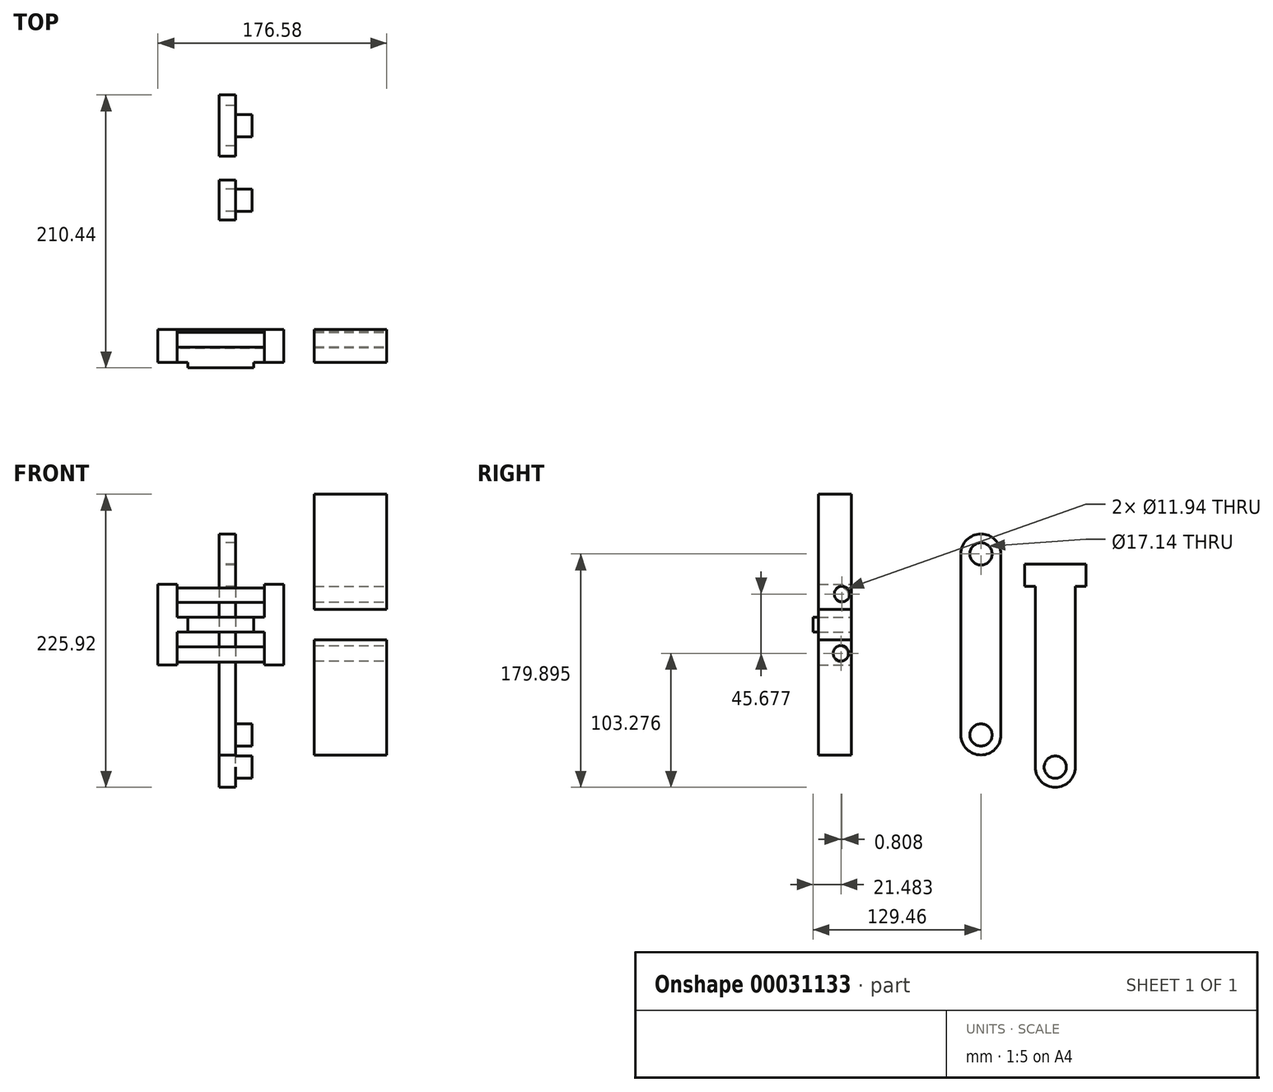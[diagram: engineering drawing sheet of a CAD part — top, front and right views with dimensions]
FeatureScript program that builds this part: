
annotation { "Feature Type Name" : "Feature", "Feature Type Description" : "" }
export const myFeature = defineFeature(function(context is Context, id is Id, definition is map)
    precondition{}
    {
        {
            var Q0;
            Q0=qCreatedBy(makeId("Front.planeOp"),FACE);
            var sketch = newSketch(context, id + "F0", { "sketchPlane" : qUnion([Q0])});
            skLineSegment(sketch, "E0.left", {"start": v(-47.09, 25.12) * mm, "end": v(-47.09, -37.18) * mm});
            skLineSegment(sketch, "E0.right", {"start": v(50.08, 25.12) * mm, "end": v(50.08, -37.18) * mm});
            skLineSegment(sketch, "E1.top", {"start": v(-32.36, -0.3) * mm, "end": v(35.17, -0.3) * mm});
            skLineSegment(sketch, "E1.left", {"start": v(-32.36, 25.12) * mm, "end": v(-32.36, -0.3) * mm});
            skLineSegment(sketch, "E1.right", {"start": v(35.17, 25.12) * mm, "end": v(35.17, -0.3) * mm});
            skLineSegment(sketch, "E2.top", {"start": v(-32.36, -11.75) * mm, "end": v(35.17, -11.75) * mm});
            skLineSegment(sketch, "E2.left", {"start": v(-32.36, -37.18) * mm, "end": v(-32.36, -11.75) * mm});
            skLineSegment(sketch, "E2.right", {"start": v(35.17, -37.18) * mm, "end": v(35.17, -11.75) * mm});
            skLineSegment(sketch, "E3", {"start": v(50.08, 25.12) * mm, "end": v(35.17, 25.12) * mm});
            skLineSegment(sketch, "E4", {"start": v(-32.36, 25.12) * mm, "end": v(-47.09, 25.12) * mm});
            skLineSegment(sketch, "E5", {"start": v(-32.36, -37.18) * mm, "end": v(-47.09, -37.18) * mm});
            skLineSegment(sketch, "E6", {"start": v(50.08, -37.18) * mm, "end": v(35.17, -37.18) * mm});
            skLineSegment(sketch, "E7.trimOffspring", {"start": v(35.17, -37.18) * mm, "end": v(50.08, -37.18) * mm});
            skLineSegment(sketch, "E8.top", {"start": v(73.53, -17.9) * mm, "end": v(129.5, -17.9) * mm});
            skLineSegment(sketch, "E8.left", {"start": v(73.53, -106.8) * mm, "end": v(73.53, -17.9) * mm});
            skLineSegment(sketch, "E8.right", {"start": v(129.5, -106.8) * mm, "end": v(129.5, -17.9) * mm});
            skLineSegment(sketch, "E9.bottom", {"start": v(129.5, 5.5) * mm, "end": v(73.53, 5.5) * mm});
            skLineSegment(sketch, "E9.top", {"start": v(129.5, 94.4) * mm, "end": v(73.53, 94.4) * mm});
            skLineSegment(sketch, "E9.left", {"start": v(129.5, 5.5) * mm, "end": v(129.5, 94.4) * mm});
            skLineSegment(sketch, "E9.right", {"start": v(73.53, 5.5) * mm, "end": v(73.53, 94.4) * mm});
            skLineSegment(sketch, "E10", {"start": v(73.53, -106.8) * mm, "end": v(129.5, -106.8) * mm});
            skSolve(sketch);
        }
        {
            var Q0;
            Q0=makeQuery(id+"F0.imprint","IMPRINT",FACE,{"disambiguationData":[TD([[makeQuery(id+"F0.imprint","IMPRINT",EDGE,{"derivedFrom":sQuery(id+"F0.wireOp",EDGE,"E0.left")}),1.0]])]});
            extrude(context, id + "F1", {"entities" : qUnion([Q0]), "depth" : 25.4 * mm});
        }
        {
            var Q0;
            Q0=qCreatedBy(makeId("Right.planeOp"),FACE);
            var sketch = newSketch(context, id + "F2", { "sketchPlane" : qUnion([Q0])});
            skLineSegment(sketch, "E11.bottom", {"start": v(84.42, 48.36) * mm, "end": v(84.42, 48.36) * mm});
            skLineSegment(sketch, "E11.left", {"start": v(84.42, 48.36) * mm, "end": v(84.42, -91.25) * mm});
            skLineSegment(sketch, "E11.right", {"start": v(115.3, 48.36) * mm, "end": v(115.3, -91.25) * mm});
            skArc(sketch, "E12", {"start": v(84.42, -91.25) * mm, "mid": v(99.86, -106.7) * mm, "end": v(115.3, -91.25) * mm});
            skCircle(sketch, "E13", {"center": v(99.86, -91.25) * mm, "radius": 8.57 * mm});
            skLineSegment(sketch, "E14.trimOffspring", {"start": v(115.3, 48.36) * mm, "end": v(115.3, 48.36) * mm});
            skArc(sketch, "E15", {"start": v(115.3, 48.36) * mm, "mid": v(99.86, 63.8) * mm, "end": v(84.42, 48.36) * mm});
            skCircle(sketch, "E16", {"center": v(99.86, 48.36) * mm, "radius": 8.57 * mm});
            skLineSegment(sketch, "E17.left", {"start": v(141.75, 23.53) * mm, "end": v(141.75, -116.09) * mm});
            skLineSegment(sketch, "E17.right", {"start": v(172.63, 23.53) * mm, "end": v(172.63, -116.09) * mm});
            skArc(sketch, "E18", {"start": v(141.75, -116.09) * mm, "mid": v(157.2, -131.53) * mm, "end": v(172.63, -116.09) * mm});
            skCircle(sketch, "E19", {"center": v(157.2, -116.09) * mm, "radius": 8.57 * mm});
            skLineSegment(sketch, "E17.bottom", {"start": v(141.75, 23.53) * mm, "end": v(141.75, 23.53) * mm});
            skLineSegment(sketch, "E20.trimOffspring", {"start": v(172.63, 23.53) * mm, "end": v(172.63, 23.53) * mm});
            skLineSegment(sketch, "E21.bottom", {"start": v(133.54, 23.53) * mm, "end": v(157.2, 23.53) * mm});
            skLineSegment(sketch, "E21.top", {"start": v(133.54, 40.41) * mm, "end": v(157.2, 40.41) * mm});
            skLineSegment(sketch, "E21.left", {"start": v(133.54, 23.53) * mm, "end": v(133.54, 40.41) * mm});
            skLineSegment(sketch, "E22.bottom", {"start": v(157.2, 23.53) * mm, "end": v(180.84, 23.53) * mm});
            skLineSegment(sketch, "E22.top", {"start": v(157.2, 40.41) * mm, "end": v(180.84, 40.41) * mm});
            skLineSegment(sketch, "E22.right", {"start": v(180.84, 23.53) * mm, "end": v(180.84, 40.41) * mm});
            skSolve(sketch);
        }
        {
            var Q0;
            Q0 = qSketchRegion(id + "F2", true);
            var Q1;
            Q1=makeQuery(id+"F2.imprint","IMPRINT",FACE,{"disambiguationData":[TD([[makeQuery(id+"F2.imprint","IMPRINT",EDGE,{"derivedFrom":sQuery(id+"F2.wireOp",EDGE,"E11.left")}),1.0]])]});
            extrude(context, id + "F3", {"entities" : qUnion([Q0, Q1]), "depth" : 12.7 * mm});
        }
        {
            var Q0;
            Q0=makeQuery(id+"F2.imprint","IMPRINT",FACE,{"disambiguationData":[TD([[makeQuery(id+"F2.imprint","IMPRINT",EDGE,{"derivedFrom":sQuery(id+"F2.wireOp",EDGE,"E13")}),1.0]])]});
            var Q1;
            Q1=makeQuery(id+"F2.imprint","IMPRINT",FACE,{"disambiguationData":[TD([[makeQuery(id+"F2.imprint","IMPRINT",EDGE,{"derivedFrom":sQuery(id+"F2.wireOp",EDGE,"E19")}),1.0]])]});
            extrude(context, id + "F4", {"entities" : qUnion([Q0, Q1]), "operationType" : NewBodyOperationType.ADD, "depth" : 25.4 * mm});
        }
        {
            var Q0;
            Q0=makeQuery(id+"F1.opExtrude","SWEPT_FACE",FACE,{"disambiguationData":[OSD([sQuery(id+"F0.wireOp",EDGE,"E2.top")])]});
            var sketch = newSketch(context, id + "F5", { "sketchPlane" : qUnion([Q0])});
            skLineSegment(sketch, "E23.bottom", {"start": v(-23.98, 29.6) * mm, "end": v(26.79, 29.6) * mm});
            skLineSegment(sketch, "E23.top", {"start": v(-23.98, 25.4) * mm, "end": v(26.79, 25.4) * mm});
            skLineSegment(sketch, "E23.left", {"start": v(-23.98, 29.6) * mm, "end": v(-23.98, 25.4) * mm});
            skLineSegment(sketch, "E23.right", {"start": v(26.79, 29.6) * mm, "end": v(26.79, 25.4) * mm});
            skLineSegment(sketch, "E24", {"start": v(15.45, 29.6) * mm, "end": v(-12.64, 29.6) * mm});
            skLineSegment(sketch, "E25", {"start": v(-12.64, 29.6) * mm, "end": v(-12.64, 92.67) * mm});
            skLineSegment(sketch, "E26", {"start": v(15.45, 29.6) * mm, "end": v(15.45, 92.67) * mm});
            skArc(sketch, "E27", {"start": v(15.45, 92.67) * mm, "mid": v(1.4, 106.72) * mm, "end": v(-12.64, 92.67) * mm});
            skCircle(sketch, "E28", {"center": v(1.4, 92.67) * mm, "radius": 8.57 * mm});
            skSolve(sketch);
        }
        {
            var Q0;
            Q0=makeQuery(id+"F5.imprint","IMPRINT",FACE,{"disambiguationData":[TD([[makeQuery(id+"F5.imprint","IMPRINT",EDGE,{"derivedFrom":sQuery(id+"F5.wireOp",EDGE,"E24")}),-1.0]])]});
            var Q1;
            Q1=makeQuery(id+"F5.imprint","IMPRINT",FACE,{"disambiguationData":[TD([[makeQuery(id+"F5.imprint","IMPRINT",EDGE,{"derivedFrom":sQuery(id+"F5.wireOp",EDGE,"E23.top")}),1.0]])]});
            extrude(context, id + "F6", {"entities" : qUnion([Q0, Q1]), "operationType" : NewBodyOperationType.ADD, "oppositeDirection" : true, "depth" : 11.44 * mm});
        }
        {
            var Q0;
            Q0=makeQuery(id+"F0.imprint","IMPRINT",FACE,{"disambiguationData":[TD([[makeQuery(id+"F0.imprint","IMPRINT",EDGE,{"derivedFrom":sQuery(id+"F0.wireOp",EDGE,"E8.top")}),-1.0]])]});
            var Q1;
            Q1=makeQuery(id+"F0.imprint","IMPRINT",FACE,{"disambiguationData":[TD([[makeQuery(id+"F0.imprint","IMPRINT",EDGE,{"derivedFrom":sQuery(id+"F0.wireOp",EDGE,"E9.bottom")}),-1.0]])]});
            extrude(context, id + "F7", {"entities" : qUnion([Q0, Q1]), "depth" : 25.4 * mm});
        }
        {
            var Q0;
            Q0=makeQuery(id+"F1.opExtrude","SWEPT_FACE",FACE,{"disambiguationData":[OSD([sQuery(id+"F0.wireOp",EDGE,"E2.left")])]});
            var sketch = newSketch(context, id + "F8", { "sketchPlane" : qUnion([Q0])});
            skCircle(sketch, "E29", {"center": v(-8.7, -29.08) * mm, "radius": 5.87 * mm});
            skCircle(sketch, "E30", {"center": v(-7.9, 16.6) * mm, "radius": 5.67 * mm});
            skSolve(sketch);
        }
        {
            var Q0;
            Q0=makeQuery(id+"F7.opExtrude","SWEPT_FACE",FACE,{"disambiguationData":[OSD([sQuery(id+"F0.wireOp",EDGE,"E8.right")])]});
            var sketch = newSketch(context, id + "F9", { "sketchPlane" : qUnion([Q0])});
            skCircle(sketch, "E31", {"center": v(-8.12, -28.25) * mm, "radius": 5.9 * mm});
            skCircle(sketch, "E32", {"center": v(-7.3, 17.42) * mm, "radius": 5.7 * mm});
            skSolve(sketch);
        }
        {
            var Q0;
            Q0=sQuery(id+"F9.wireOp",VERTEX,"E31.center");
            var Q1;
            Q1=sQuery(id+"F9.wireOp",VERTEX,"E32.center");
            var Q2;
            Q2=makeQuery(id+"F7.opExtrude","SWEPT_BODY",BODY,{"disambiguationData":[OSD([sQuery(id+"F0.wireOp",EDGE,"E8.top"),sQuery(id+"F0.wireOp",EDGE,"E8.left"),sQuery(id+"F0.wireOp",EDGE,"E8.right"),sQuery(id+"F0.wireOp",EDGE,"E10")])]});
            var Q3;
            Q3=makeQuery(id+"F7.opExtrude","SWEPT_BODY",BODY,{"disambiguationData":[OSD([sQuery(id+"F0.wireOp",EDGE,"E9.bottom"),sQuery(id+"F0.wireOp",EDGE,"E9.top"),sQuery(id+"F0.wireOp",EDGE,"E9.left"),sQuery(id+"F0.wireOp",EDGE,"E9.right")])]});
            hole(context, id + "F10", {"style" : HoleStyle.SIMPLE, "holeDiameter" : 11.94 * mm, "endStyle" : HoleEndStyle.BLIND, "holeDepth" : 76.2 * mm, "locations" : qUnion([Q0, Q1]), "scope" : qUnion([Q2, Q3])});
        }
        {
            var Q0;
            Q0=makeQuery(id+"F8.imprint","IMPRINT",FACE,{"disambiguationData":[TD([[makeQuery(id+"F8.imprint","IMPRINT",EDGE,{"derivedFrom":sQuery(id+"F8.wireOp",EDGE,"E30")}),1.0]])]});
            var Q1;
            Q1=makeQuery(id+"F8.imprint","IMPRINT",FACE,{"disambiguationData":[TD([[makeQuery(id+"F8.imprint","IMPRINT",EDGE,{"derivedFrom":sQuery(id+"F8.wireOp",EDGE,"E29")}),1.0]])]});
            var Q2;
            Q2=sQuery(id+"F8.wireOp",EDGE,"E29");
            var Q3;
            Q3=sQuery(id+"F8.wireOp",EDGE,"E30");
            extrude(context, id + "F11", {"entities" : qUnion([Q0, Q1]), "operationType" : NewBodyOperationType.ADD, "surfaceEntities" : qUnion([Q2, Q3]), "depth" : 76.2 * mm});
        }
    });
